FCSTD DOCUMENT  (FreeCAD 0.19R)
Label: folding
License: Creative Commons Attribution-ShareAlike
LicenseURL: http://creativecommons.org/licenses/by-sa/4.0/
objects: Sketcher::SketchObject×11, TechDraw::DrawViewPart×5, PartDesign::Plane×5, TechDraw::DrawSVGTemplate×3, TechDraw::DrawPage×3, PartDesign::SubShapeBinder×2, PartDesign::Body×1
note: 19 computed .brp shape members not serialized (recipe doc carries the construction recipe); baked Part::Feature solids carry a one-line shape summary decoded from their .brp

FEATURE [Sketcher::SketchObject] Sketch  label="outline"
  MapMode = 5
  Support = -> [XY_Plane]
  sketch-geometry (4):
    g0: LineSegment StartX=-70 StartY=70 StartZ=0 EndX=70 EndY=70 EndZ=0
    g1: LineSegment StartX=70 StartY=70 StartZ=0 EndX=70 EndY=-70 EndZ=0
    g2: LineSegment StartX=70 StartY=-70 StartZ=0 EndX=-70 EndY=-70 EndZ=0
    g3: LineSegment StartX=-70 StartY=-70 StartZ=0 EndX=-70 EndY=70 EndZ=0
  constraints (11):
    c: Coincident(g0,g1)
    c: Coincident(g1,g2)
    c: Coincident(g2,g3)
    c: Coincident(g3,g0)
    c: Horizontal(g0)
    c: Horizontal(g2)
    c: Vertical(g1)
    c: Vertical(g3)
    c: Equal(g2,g1)
    c: DistanceX(g0,g0) = 140  'width'
    c: Symmetric(g2,g0,g-1)
FEATURE [Sketcher::SketchObject] Sketch001  label="folds_2"
  ExternalGeometry = -> [Sketch]
  MapMode = 5
  Support = -> [XY_Plane]
  sketch-geometry (8):
    g0: LineSegment StartX=2e-16 StartY=70 StartZ=0 EndX=-60 EndY=-70 EndZ=0
    g1: LineSegment StartX=60 StartY=70 StartZ=0 EndX=0 EndY=-70 EndZ=0
    g2: LineSegment StartX=2e-16 StartY=70 StartZ=0 EndX=60 EndY=70 EndZ=0
    g3: LineSegment StartX=60 StartY=70 StartZ=0 EndX=70 EndY=70 EndZ=0
    g4: LineSegment StartX=-70 StartY=70 StartZ=0 EndX=0 EndY=70 EndZ=0
    g5: LineSegment StartX=-70 StartY=-70 StartZ=0 EndX=-60 EndY=-70 EndZ=0
    g6: LineSegment StartX=-60 StartY=-70 StartZ=0 EndX=0 EndY=-70 EndZ=0
    g7: LineSegment StartX=0 StartY=-70 StartZ=0 EndX=70 EndY=-70 EndZ=0
  constraints (21):
    c: Coincident(g2,g0)
    c: Coincident(g2,g1)
    c: Horizontal(g2)
    c: Coincident(g3,g1)
    c: Horizontal(g3)
    c: Coincident(g4,g0)
    c: Horizontal(g5)
    c: Coincident(g5,g6)
    c: Horizontal(g6)
    c: Coincident(g6,g7)
    c: Coincident(g4,g-3)
    c: Coincident(g3,g-4)
    c: Coincident(g5,g0)
    c: Coincident(g1,g6)
    c: Coincident(g5,g-3)
    c: Coincident(g7,g-4)
    c: Equal(g5,g3)
    c: Equal(g6,g2)
    c: Equal(g4,g7)
    c: PointOnObject(g0,g-2)
    c: DistanceX(g3,g3) = 10
FEATURE [Sketcher::SketchObject] Sketch002  label="folds_1"
  ExternalGeometry = -> [Sketch,Sketch001]
  MapMode = 5
  Support = -> [XY_Plane]
  sketch-geometry (6):
    g0: LineSegment StartX=2e-16 StartY=70 StartZ=0 EndX=-70 EndY=0 EndZ=0
    g1: LineSegment StartX=0 StartY=-70 StartZ=0 EndX=70 EndY=0 EndZ=0
    g2: LineSegment StartX=-30 StartY=1.8e-15 StartZ=0 EndX=0 EndY=-70 EndZ=0
    g3: LineSegment StartX=-50.6897 StartY=-48.2759 StartZ=0 EndX=0 EndY=-70 EndZ=0
    g4: LineSegment StartX=2e-16 StartY=70 StartZ=0 EndX=50.6897 EndY=48.2759 EndZ=0
    g5: LineSegment StartX=2e-16 StartY=70 StartZ=0 EndX=30 EndY=0 EndZ=0
  constraints (12):
    c: Symmetric(g-3,g-3,g0)
    c: Coincident(g0,g-5)
    c: Symmetric(g-4,g-4,g1)
    c: Coincident(g1,g-6)
    c: Coincident(g3,g2)
    c: Coincident(g5,g4)
    c: Symmetric(g-6,g-6,g5)
    c: Coincident(g4,g0)
    c: Coincident(g2,g1)
    c: Symmetric(g-5,g-5,g2)
    c: Perpendicular(g3,g-5) = 4.71239
    c: Perpendicular(g4,g-6) = 4.71239
FEATURE [Sketcher::SketchObject] Sketch003  label="visible_area_1"
  ExternalGeometry = -> [Sketch,Sketch002,Sketch001]
  MapMode = 5
  Support = -> [XY_Plane]
  sketch-geometry (15):
    g0: LineSegment StartX=30 StartY=0 StartZ=0 EndX=70 EndY=1.42e-14 EndZ=0
    g1: LineSegment StartX=70 StartY=1.42e-14 StartZ=0 EndX=70 EndY=14.8792 EndZ=0
    g2: LineSegment StartX=70 StartY=14.8792 StartZ=0 EndX=30 EndY=-1.8e-15 EndZ=0
    g3: LineSegment StartX=30 StartY=0 StartZ=0 EndX=50.6897 EndY=48.2759 EndZ=0
    g4: LineSegment StartX=50.6897 StartY=48.2759 StartZ=0 EndX=70 EndY=40 EndZ=0
    g5: LineSegment StartX=30 StartY=0 StartZ=0 EndX=41.3793 EndY=26.5517 EndZ=0
    g6: LineSegment StartX=41.3793 StartY=26.5517 StartZ=0 EndX=57.471 EndY=26.5517 EndZ=0
    g7: LineSegment StartX=57.471 StartY=26.5517 StartZ=0 EndX=70 EndY=40 EndZ=0
    g8: LineSegment StartX=70 StartY=40 StartZ=0 EndX=70 EndY=14.8792 EndZ=0
    g9: LineSegment StartX=101.379 StartY=26.5517 StartZ=0 EndX=57.471 EndY=26.5517 EndZ=0
    g10: LineSegment StartX=101.379 StartY=26.5517 StartZ=0 EndX=30 EndY=0 EndZ=0
    g11: LineSegment StartX=70 StartY=40 StartZ=0 EndX=101.379 EndY=26.5517 EndZ=0
    g12: LineSegment StartX=57.471 StartY=26.5517 StartZ=0 EndX=70 EndY=14.8792 EndZ=0
    g13: LineSegment StartX=30 StartY=0 StartZ=0 EndX=30 EndY=60 EndZ=0
    g14: LineSegment StartX=-30 StartY=0 StartZ=0 EndX=30 EndY=0 EndZ=0
  constraints (44):
    c: Coincident(g0,g1)
    c: Coincident(g1,g2)
    c: Coincident(g2,g0)
    c: Coincident(g0,g-6)
    c: PointOnObject(g1,g-3)
    c: Coincident(g0,g-9)
    c: Coincident(g3,g0)
    c: Coincident(g3,g-5)
    c: PointOnObject(g4,g-3)
    c: Parallel(g4,g-5)
    c: Coincident(g4,g3)
    c: Coincident(g0,g5)
    c: Coincident(g5,g6)
    c: Horizontal(g6)
    c: Coincident(g6,g7)
    c: Coincident(g7,g4)
    c: Coincident(g7,g8)
    c: Coincident(g8,g1)
    c: Horizontal(g9)
    c: Coincident(g9,g6)
    c: PointOnObject(g5,g3)
    c: Coincident(g10,g9)
    c: Coincident(g10,g0)
    c: Equal(g10,g-9)
    c: Coincident(g11,g7)
    c: Coincident(g11,g9)
    c: Parallel(g11,g4)
    c: Coincident(g12,g6)
    c: Coincident(g12,g1)
    c: Angle(g-3,g11) = 1.1659
    c: Angle(g4,g7) = 1.22566
    c: Perpendicular(g12,g7)
    c: Angle(g-8,g-9) = 0.809784
    c: Angle(g-9,g-1) = 1.1659
    c: Angle(g5,g-9) = 0.809784
    c: Angle(g2,g1) = 1.21468
    c: Angle(g11,g10) = 0.761013
    c: Coincident(g13,g0)
    c: Vertical(g13)
    c: Horizontal(g14)
    c: Coincident(g14,g0)
    c: PointOnObject(g14,g-8)
    c: Equal(g14,g13)
    c: PointOnObject(g1,g10)
FEATURE [Sketcher::SketchObject] Sketch004  label="visible_area_2"
  ExternalGeometry = -> [Sketch002,Sketch,Sketch003]
  MapMode = 5
  Support = -> [XY_Plane]
  sketch-geometry (14):
    g0: LineSegment StartX=30 StartY=0 StartZ=0 EndX=70 EndY=-40 EndZ=0
    g1: LineSegment StartX=70 StartY=0 StartZ=0 EndX=70 EndY=-40 EndZ=0
    g2: LineSegment StartX=70 StartY=-40 StartZ=0 EndX=50 EndY=-20 EndZ=0
    g3: LineSegment StartX=50 StartY=-20 StartZ=0 EndX=70 EndY=0 EndZ=0
    g4: LineSegment StartX=70 StartY=-40 StartZ=0 EndX=41.9536 EndY=-28.0464 EndZ=0
    g5: LineSegment StartX=41.9536 StartY=-28.0464 StartZ=0 EndX=50 EndY=-20 EndZ=0
    g6: LineSegment StartX=30 StartY=70 StartZ=0 EndX=30 EndY=0 EndZ=0
    g7: LineSegment StartX=41.3793 StartY=26.5517 StartZ=0 EndX=30 EndY=26.5517 EndZ=0
    g8: LineSegment StartX=0 StartY=70 StartZ=0 EndX=30 EndY=70 EndZ=0
    g9: LineSegment StartX=30 StartY=70 StartZ=0 EndX=30 EndY=57.1429 EndZ=0
    g10: LineSegment StartX=30 StartY=57.1429 StartZ=0 EndX=0 EndY=70 EndZ=0
    g11: LineSegment StartX=0 StartY=70 StartZ=0 EndX=21.4286 EndY=48.5714 EndZ=0
    g12: LineSegment StartX=21.4286 StartY=48.5714 StartZ=0 EndX=30 EndY=57.1429 EndZ=0
    g13: LineSegment StartX=21.4286 StartY=48.5714 StartZ=0 EndX=12.8571 EndY=40 EndZ=0
  constraints (35):
    c: Coincident(g0,g-3)
    c: PointOnObject(g0,g-4)
    c: Perpendicular(g0,g-5)
    c: Coincident(g1,g2)
    c: Coincident(g2,g3)
    c: Coincident(g3,g1)
    c: Coincident(g1,g-5)
    c: Coincident(g1,g0)
    c: PointOnObject(g2,g-5)
    c: PointOnObject(g2,g0)
    c: Coincident(g1,g4)
    c: Coincident(g4,g5)
    c: Coincident(g5,g2)
    c: PointOnObject(g4,g-5)
    c: Coincident(g6,g0)
    c: Perpendicular(g6,g-7) = 1.5708
    c: Coincident(g7,g-8)
    c: Horizontal(g7)
    c: PointOnObject(g7,g6)
    c: Equal(g7,g5)
    c: Coincident(g-6,g8)
    c: Coincident(g8,g6)
    c: Coincident(g8,g9)
    c: PointOnObject(g9,g-6)
    c: Coincident(g9,g10)
    c: Coincident(g10,g8)
    c: PointOnObject(g9,g6)
    c: Coincident(g8,g11)
    c: Coincident(g11,g12)
    c: Coincident(g12,g9)
    c: Coincident(g13,g11)
    c: Parallel(g12,g13)
    c: PointOnObject(g13,g-3)
    c: Equal(g12,g13)
    c: Perpendicular(g11,g12)
FEATURE [TechDraw::DrawSVGTemplate] Template
  Height = 300
  Orientation = 1
  Width = 300
FEATURE [TechDraw::DrawViewPart] View  label="folding_View"
  CoarseView = false
  Direction = (0,0,1)
  Focus = 100
  HardHidden = false
  IsoCount = 0
  IsoHidden = false
  IsoVisible = false
  LockPosition = false
  Perspective = false
  Rotation = 0
  ScaleType = 0
  SeamHidden = false
  SeamVisible = true
  SmoothHidden = false
  SmoothVisible = true
  Source = -> [Sketch,Sketch004,Sketch003,Sketch002,Sketch001]
  X = 150
  XDirection = (1,0,0)
  Y = 150
FEATURE [TechDraw::DrawPage] Page  label="folding_export"
  KeepUpdated = true
  NextBalloonIndex = 1
  ProjectionType = 0
  Template = -> Template
  Views = -> [View]
FEATURE [TechDraw::DrawSVGTemplate] Template001
  Height = 140
  Orientation = 1
  Width = 140
FEATURE [TechDraw::DrawSVGTemplate] Template002
  Height = 140
  Orientation = 1
  Width = 140
FEATURE [TechDraw::DrawViewPart] View002  label="outline_View"
  CoarseView = false
  Direction = (0,0,1)
  Focus = 100
  HardHidden = false
  IsoCount = 0
  IsoHidden = false
  IsoVisible = false
  LockPosition = false
  Perspective = false
  Rotation = 0
  ScaleType = 0
  SeamHidden = false
  SeamVisible = true
  SmoothHidden = false
  SmoothVisible = true
  Source = -> [Sketch]
  X = 70
  XDirection = (1,0,0)
  Y = 70
FEATURE [TechDraw::DrawViewPart] View003  label="folds_2_View"
  CoarseView = false
  Direction = (0,0,1)
  Focus = 100
  HardHidden = false
  IsoCount = 0
  IsoHidden = false
  IsoVisible = false
  LockPosition = false
  Perspective = false
  Rotation = 0
  ScaleType = 0
  SeamHidden = false
  SeamVisible = true
  SmoothHidden = false
  SmoothVisible = true
  Source = -> [Sketch001]
  X = 70
  XDirection = (1,0,0)
  Y = 70
FEATURE [TechDraw::DrawPage] Page002  label="folds_2_export"
  KeepUpdated = true
  NextBalloonIndex = 1
  ProjectionType = 0
  Template = -> Template002
  Views = -> [View002,View003]
FEATURE [TechDraw::DrawViewPart] View005  label="outline_View001"
  CoarseView = false
  Direction = (0,0,1)
  Focus = 100
  HardHidden = false
  IsoCount = 0
  IsoHidden = false
  IsoVisible = false
  LockPosition = false
  Perspective = false
  Rotation = 0
  ScaleType = 0
  SeamHidden = false
  SeamVisible = true
  SmoothHidden = false
  SmoothVisible = true
  Source = -> [Sketch]
  X = 70
  XDirection = (1,0,0)
  Y = 70
FEATURE [TechDraw::DrawViewPart] View006  label="folds_1_View"
  CoarseView = false
  Direction = (0,0,1)
  Focus = 100
  HardHidden = false
  IsoCount = 0
  IsoHidden = false
  IsoVisible = false
  LockPosition = false
  Perspective = false
  Rotation = 0
  ScaleType = 0
  SeamHidden = false
  SeamVisible = true
  SmoothHidden = false
  SmoothVisible = true
  Source = -> [Sketch002]
  X = 70
  XDirection = (1,0,0)
  Y = 70
FEATURE [TechDraw::DrawPage] Page001  label="folds_1_export"
  KeepUpdated = true
  NextBalloonIndex = 1
  ProjectionType = 0
  Template = -> Template001
  Views = -> [View005,View006]
FEATURE [PartDesign::SubShapeBinder] Binder  label="visible_area_1_Binder"
  BindMode = 0
  ClaimChildren = false
  Context = -> Body [Binder.]
  Fuse = false
  MakeFace = true
  PartialLoad = false
  Placement = pos=(0,0,0) rot=(0,0,1;3.14159rad)
  Relative = true
  Support = -> [Sketch003]
  _Version = 2
FEATURE [PartDesign::SubShapeBinder] Binder001  label="visible_area_2_Binder"
  BindMode = 0
  ClaimChildren = false
  Context = -> Body [Binder001.]
  Fuse = false
  MakeFace = true
  PartialLoad = false
  Placement = pos=(0,0,0) rot=(0,0,1;3.14159rad)
  Relative = true
  Support = -> [Sketch004]
  _Version = 2
FEATURE [PartDesign::Plane] DatumPlane  label="t1s1.1_DatumPlane"
  Length = 237.588
  MapMode = 49
  Placement = pos=(-50,20,0) rot=(0,0,-1;0.785398rad)
  ResizeMode = 0
  Support = -> [Binder001]
  Width = 237.588
FEATURE [Sketcher::SketchObject] Sketch005  label="t1s1.1"
  ExternalGeometry = -> [Binder001]
  MapMode = 5
  Placement = pos=(-50,20,0) rot=(0,0,-1;0.785398rad)
  Support = -> [DatumPlane]
  sketch-geometry (3):
    g0: LineSegment StartX=-28.2843 StartY=0 StartZ=0 EndX=0 EndY=0 EndZ=0
    g1: LineSegment StartX=0 StartY=0 StartZ=0 EndX=0 EndY=11.3793 EndZ=0
    g2: LineSegment StartX=0 StartY=11.3793 StartZ=0 EndX=-28.2843 EndY=0 EndZ=0
  constraints (6):
    c: Coincident(g0,g1)
    c: Coincident(g1,g2)
    c: Coincident(g2,g0)
    c: Coincident(g0,g-1)
    c: Coincident(g0,g-3)
    c: Coincident(g1,g-3)
FEATURE [PartDesign::Plane] DatumPlane001  label="t1s1.4_DatumPlane"
  AttachmentOffset = pos=(0,0,0) rot=(0,0,1;3.14159rad)
  Length = 237.588
  MapMode = 49
  Placement = pos=(50,-20,0) rot=(0,0,1;5.49779rad)
  ResizeMode = 0
  Support = -> [Sketch004]
  Width = 237.588
FEATURE [Sketcher::SketchObject] Sketch006  label="t1s1.4"
  ExternalGeometry = -> [Sketch004]
  MapMode = 5
  Placement = pos=(50,-20,0) rot=(0,0,-1;0.785398rad)
  Support = -> [DatumPlane001]
  sketch-geometry (3):
    g0: LineSegment StartX=0 StartY=0 StartZ=0 EndX=0 EndY=28.2843 EndZ=0
    g1: LineSegment StartX=0 StartY=28.2843 StartZ=0 EndX=28.2843 EndY=0 EndZ=0
    g2: LineSegment StartX=28.2843 StartY=0 StartZ=0 EndX=0 EndY=0 EndZ=0
  constraints (6):
    c: Coincident(g-1,g0)
    c: Coincident(g0,g1)
    c: Coincident(g1,g2)
    c: Coincident(g2,g0)
    c: Coincident(g0,g-3)
    c: Coincident(g1,g-3)
FEATURE [PartDesign::Plane] DatumPlane002  label="t1s1.5_DatumPlane"
  Length = 237.588
  MapMode = 51
  Placement = pos=(70,0,0) rot=(0,0,-1;0.785398rad)
  ResizeMode = 0
  Support = -> [Sketch002]
  Width = 237.588
FEATURE [Sketcher::SketchObject] Sketch007  label="t1s1.5"
  ExternalGeometry = -> [Sketch003]
  MapMode = 5
  Placement = pos=(70,-7.1e-15,0) rot=(0,0,-1;0.785398rad)
  Support = -> [DatumPlane002]
  sketch-geometry (3):
    g0: LineSegment StartX=0 StartY=0 StartZ=0 EndX=-28.2843 EndY=-28.2843 EndZ=0
    g1: LineSegment StartX=-28.2843 StartY=-28.2843 StartZ=0 EndX=-10.5212 EndY=10.5212 EndZ=0
    g2: LineSegment StartX=-10.5212 StartY=10.5212 StartZ=0 EndX=0 EndY=0 EndZ=0
  constraints (6):
    c: Coincident(g0,g1)
    c: Coincident(g1,g2)
    c: Coincident(g2,g0)
    c: Coincident(g0,g-1)
    c: Coincident(g1,g-3)
    c: Coincident(g0,g-3)
FEATURE [PartDesign::Plane] DatumPlane003  label="t1s2.6_DatumPlane"
  Length = 237.588
  MapMode = 49
  Placement = pos=(21.4286,48.5714,0) rot=(0,0,1;0.785398rad)
  ResizeMode = 0
  Support = -> [Sketch004]
  Width = 237.588
FEATURE [Sketcher::SketchObject] Sketch008  label="t1s2.6"
  ExternalGeometry = -> [Sketch002,Sketch004]
  MapMode = 5
  Placement = pos=(21.4286,48.5714,0) rot=(0,0,1;0.785398rad)
  Support = -> [DatumPlane003]
  sketch-geometry (3):
    g0: LineSegment StartX=0 StartY=0 StartZ=0 EndX=0 EndY=30.3046 EndZ=0
    g1: LineSegment StartX=0 StartY=30.3046 StartZ=0 EndX=12.1218 EndY=0 EndZ=0
    g2: LineSegment StartX=12.1218 StartY=0 StartZ=0 EndX=0 EndY=0 EndZ=0
  constraints (6):
    c: Coincident(g-1,g0)
    c: Coincident(g0,g1)
    c: Coincident(g1,g2)
    c: Coincident(g2,g0)
    c: Coincident(g1,g-4)
    c: Coincident(g0,g-3)
FEATURE [PartDesign::Plane] DatumPlane004  label="t1s3.3_DatumPlane004"
  Length = 168
  MapMode = 49
  Placement = pos=(30,70,0) rot=(0,0,-1;1.5708rad)
  ResizeMode = 0
  Support = -> [Sketch004]
  Width = 168
FEATURE [Sketcher::SketchObject] Sketch009  label="t1s3.3"
  ExternalGeometry = -> [Sketch004]
  MapMode = 5
  Placement = pos=(30,70,0) rot=(0,0,-1;1.5708rad)
  Support = -> [DatumPlane004]
  sketch-geometry (3):
    g0: LineSegment StartX=0 StartY=0 StartZ=0 EndX=12.8571 EndY=-3.6e-15 EndZ=0
    g1: LineSegment StartX=12.8571 StartY=-3.6e-15 StartZ=0 EndX=0 EndY=-30 EndZ=0
    g2: LineSegment StartX=0 StartY=-30 StartZ=0 EndX=0 EndY=0 EndZ=0
  constraints (6):
    c: Coincident(g-1,g0)
    c: Coincident(g0,g1)
    c: Coincident(g1,g2)
    c: Coincident(g2,g0)
    c: Coincident(g0,g-3)
    c: Coincident(g1,g-3)
FEATURE [Sketcher::SketchObject] Sketch010
  ExternalGeometry = -> [Sketch003,Sketch002]
  MapMode = 5
  Support = -> [XY_Plane]
  sketch-geometry (4):
    g0: LineSegment StartX=30 StartY=57.1429 StartZ=0 EndX=30 EndY=0 EndZ=0
    g1: LineSegment StartX=30 StartY=0 StartZ=0 EndX=101.379 EndY=26.5517 EndZ=0
    g2: LineSegment StartX=101.379 StartY=26.5517 StartZ=0 EndX=30 EndY=57.1429 EndZ=0
    g3: LineSegment StartX=30 StartY=26.5517 StartZ=0 EndX=41.3793 EndY=26.5517 EndZ=0
  constraints (12):
    c: Coincident(g0,g1)
    c: Coincident(g1,g2)
    c: Coincident(g0,g2)
    c: Vertical(g0)
    c: Coincident(g0,g-4)
    c: PointOnObject(g0,g-5)
    c: Parallel(g2,g-5)
    c: Parallel(g-4,g1)
    c: Coincident(g3,g-3)
    c: Perpendicular(g3,g0) = 4.71239
    c: Angle(g1,g0) = 1.21468
    c: Angle(g0,g2) = 1.1659
FEATURE [PartDesign::Body] Body  label="folding_sketches"
  Group = -> [Sketch,Sketch002,Sketch001,Sketch003,Binder,Sketch004,Binder001,DatumPlane,Sketch005,DatumPlane001,Sketch006,DatumPlane002,Sketch007,DatumPlane003,Sketch008,DatumPlane004,Sketch009,Sketch010]
  Origin = -> Origin
